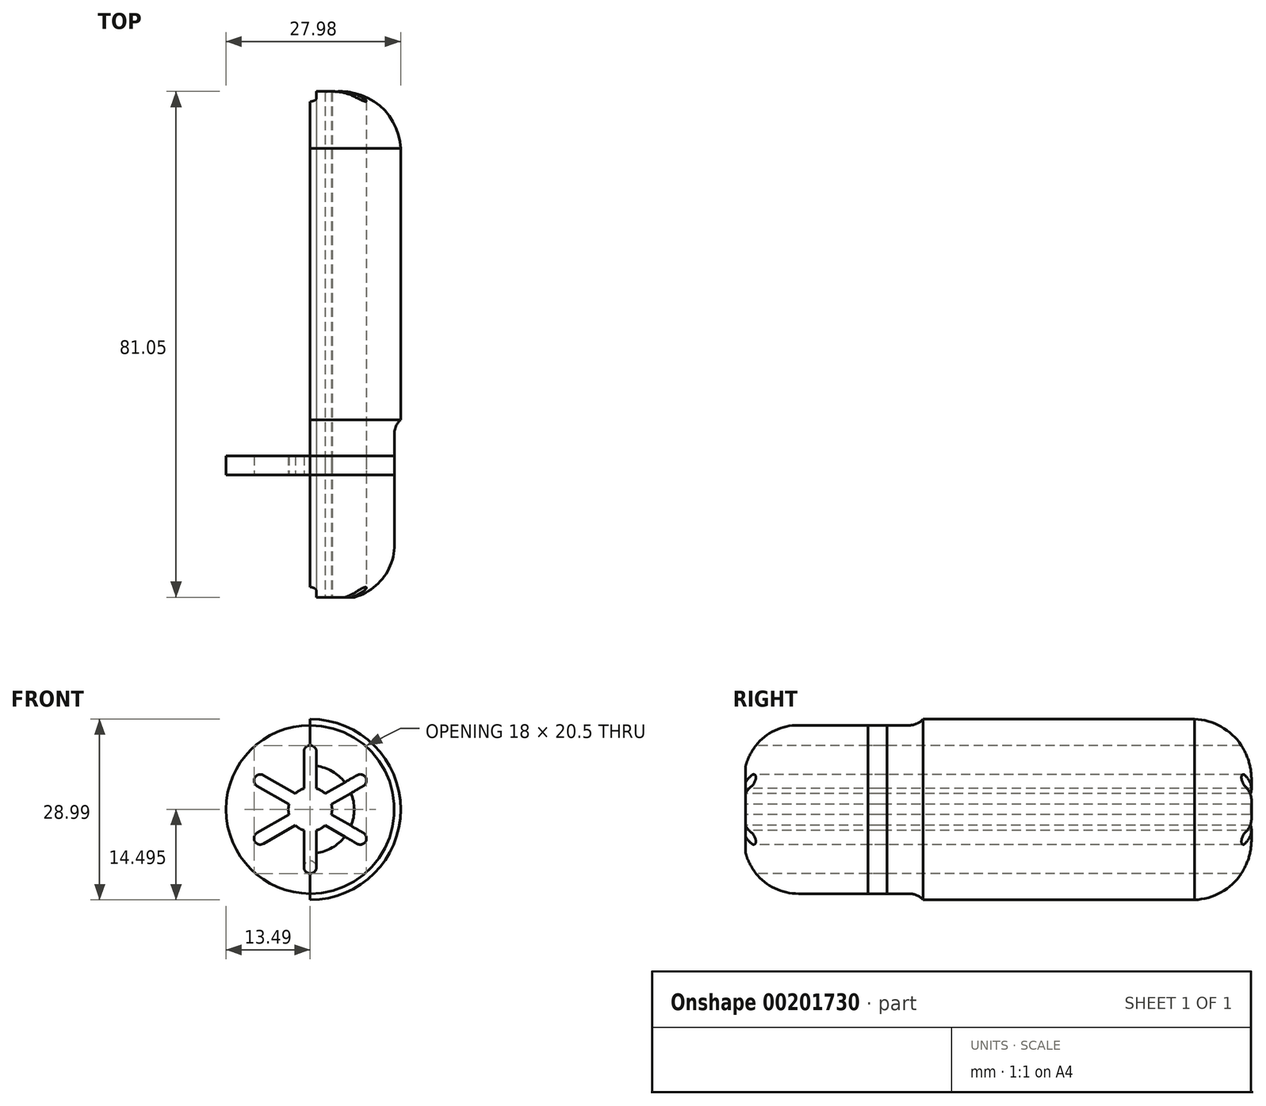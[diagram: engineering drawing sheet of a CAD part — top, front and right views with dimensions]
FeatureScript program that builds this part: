
annotation { "Feature Type Name" : "Feature", "Feature Type Description" : "" }
export const myFeature = defineFeature(function(context is Context, id is Id, definition is map)
    precondition{}
    {
        {
            var Q0;
            Q0=qCreatedBy(makeId("Right.planeOp"),FACE);
            var sketch = newSketch(context, id + "F0", { "sketchPlane" : qUnion([Q0])});
            skLineSegment(sketch, "E0.bottom", {"start": v(-3.13, 33.38) * mm, "end": v(86.87, 33.38) * mm});
            skLineSegment(sketch, "E0.top", {"start": v(-3.13, 32.38) * mm, "end": v(4.08, 32.38) * mm});
            skLineSegment(sketch, "E0.left", {"start": v(-3.13, 33.38) * mm, "end": v(-3.13, 32.38) * mm});
            skLineSegment(sketch, "E0.right", {"start": v(86.87, 33.38) * mm, "end": v(86.87, 32.38) * mm});
            skPoint(sketch, "E0.middle", {"position": v(41.87, 32.88) * mm});
            skLineSegment(sketch, "E1.bottom", {"start": v(86.87, 32.38) * mm, "end": v(81.87, 32.38) * mm, "construction": true});
            skLineSegment(sketch, "E1.top", {"start": v(86.87, 21.38) * mm, "end": v(85.87, 21.38) * mm});
            skLineSegment(sketch, "E1.left", {"start": v(86.87, 32.38) * mm, "end": v(86.87, 21.38) * mm, "construction": true});
            skLineSegment(sketch, "E1.right", {"start": v(81.87, 32.38) * mm, "end": v(81.87, 21.38) * mm, "construction": true});
            skLineSegment(sketch, "E2.bottom", {"start": v(81.87, 32.38) * mm, "end": v(71.87, 32.38) * mm, "construction": true});
            skLineSegment(sketch, "E2.top", {"start": v(81.87, 21.38) * mm, "end": v(71.87, 21.38) * mm, "construction": true});
            skLineSegment(sketch, "E2.right", {"start": v(71.87, 33.38) * mm, "end": v(71.87, 21.38) * mm, "construction": true});
            skLineSegment(sketch, "E3.0", {"start": v(85.87, 22.38) * mm, "end": v(85.37, 22.38) * mm, "construction": true});
            skLineSegment(sketch, "E4.0", {"start": v(85.87, 32.38) * mm, "end": v(85.87, 21.38) * mm, "construction": true});
            skArc(sketch, "E5", {"start": v(82.3, 22.38) * mm, "mid": v(80.84, 28.3) * mm, "end": v(76.33, 32.38) * mm});
            skArc(sketch, "E6", {"start": v(81.87, 21.38) * mm, "mid": v(79.3, 29.1) * mm, "end": v(71.87, 32.38) * mm});
            skLineSegment(sketch, "E7.trimOffspring", {"start": v(76.33, 32.38) * mm, "end": v(86.87, 32.38) * mm});
            skLineSegment(sketch, "E8.top", {"start": v(86.87, 25.38) * mm, "end": v(85.87, 25.38) * mm});
            skLineSegment(sketch, "E8.left", {"start": v(86.87, 23.38) * mm, "end": v(86.87, 25.38) * mm});
            skLineSegment(sketch, "E8.right", {"start": v(85.87, 22.38) * mm, "end": v(85.87, 22.72) * mm, "construction": true});
            skLineSegment(sketch, "E9.bottom", {"start": v(-3.13, 32.38) * mm, "end": v(-2.13, 32.38) * mm, "construction": true});
            skLineSegment(sketch, "E9.top", {"start": v(-3.13, 21.38) * mm, "end": v(-2.13, 21.38) * mm});
            skLineSegment(sketch, "E9.left", {"start": v(-3.13, 32.38) * mm, "end": v(-3.13, 21.38) * mm, "construction": true});
            skLineSegment(sketch, "E9.right", {"start": v(-2.13, 32.38) * mm, "end": v(-2.13, 21.38) * mm, "construction": true});
            skLineSegment(sketch, "E10.bottom", {"start": v(-2.13, 32.38) * mm, "end": v(4.08, 32.38) * mm, "construction": true});
            skLineSegment(sketch, "E10.top", {"start": v(-2.13, 33.38) * mm, "end": v(8.87, 33.38) * mm, "construction": true});
            skLineSegment(sketch, "E10.left", {"start": v(-2.13, 32.38) * mm, "end": v(-2.13, 33.38) * mm, "construction": true});
            skLineSegment(sketch, "E10.right", {"start": v(8.87, 32.38) * mm, "end": v(8.87, 33.38) * mm, "construction": true});
            skArc(sketch, "E11", {"start": v(4.08, 32.38) * mm, "mid": v(-1.17, 27.96) * mm, "end": v(-3.13, 21.38) * mm});
            skArc(sketch, "E12", {"start": v(8.87, 32.38) * mm, "mid": v(1.1, 29.16) * mm, "end": v(-2.13, 21.38) * mm});
            skLineSegment(sketch, "E13.trimOffspring", {"start": v(8.87, 32.38) * mm, "end": v(71.87, 32.38) * mm});
            skLineSegment(sketch, "E14", {"start": v(8.87, 21.38) * mm, "end": v(71.87, 21.38) * mm, "construction": true});
            skLineSegment(sketch, "E15.0", {"start": v(8.87, 17.38) * mm, "end": v(71.87, 17.38) * mm, "construction": true});
            skLineSegment(sketch, "E16.0", {"start": v(86.87, 23.38) * mm, "end": v(85.87, 23.38) * mm, "construction": true});
            skLineSegment(sketch, "E17.0", {"start": v(83.87, 21.38) * mm, "end": v(83.87, 25.38) * mm, "construction": true});
            skLineSegment(sketch, "E18", {"start": v(86.87, 23.38) * mm, "end": v(83.87, 21.38) * mm});
            skLineSegment(sketch, "E19.0", {"start": v(85.87, 23.92) * mm, "end": v(83.57, 22.38) * mm});
            skLineSegment(sketch, "E20.trimOffspring", {"start": v(83.87, 21.38) * mm, "end": v(81.87, 21.38) * mm});
            skLineSegment(sketch, "E21.trimOffspring", {"start": v(83.57, 22.38) * mm, "end": v(82.3, 22.38) * mm});
            skLineSegment(sketch, "E22.trimOffspring", {"start": v(85.87, 23.92) * mm, "end": v(85.87, 25.38) * mm});
            skLineSegment(sketch, "E23.bottom", {"start": v(8.87, 17.38) * mm, "end": v(-3.13, 17.38) * mm, "construction": true});
            skLineSegment(sketch, "E23.top", {"start": v(8.87, 21.38) * mm, "end": v(-3.13, 21.38) * mm, "construction": true});
            skLineSegment(sketch, "E23.left", {"start": v(8.87, 17.38) * mm, "end": v(8.87, 21.38) * mm, "construction": true});
            skLineSegment(sketch, "E23.right", {"start": v(-3.13, 17.38) * mm, "end": v(-3.13, 21.38) * mm, "construction": true});
            skSolve(sketch);
        }
        {
            var Q0;
            Q0=qCreatedBy(makeId("Right.planeOp"),FACE);
            var sketch = newSketch(context, id + "F1", { "sketchPlane" : qUnion([Q0])});
            skLineSegment(sketch, "E24.bottom", {"start": v(-3.13, 33.38) * mm, "end": v(28.58, 33.38) * mm, "construction": true});
            skLineSegment(sketch, "E24.left", {"start": v(-3.13, 33.38) * mm, "end": v(-3.13, 23.38) * mm, "construction": true});
            skLineSegment(sketch, "E24.right", {"start": v(28.58, 33.38) * mm, "end": v(28.58, 33.38) * mm});
            skLineSegment(sketch, "E25", {"start": v(28.58, 32.38) * mm, "end": v(8.84, 32.38) * mm, "construction": true});
            skArc(sketch, "E26", {"start": v(8.84, 32.38) * mm, "mid": v(1.84, 29.83) * mm, "end": v(-1.88, 23.38) * mm, "construction": true});
            skLineSegment(sketch, "E27.0", {"start": v(27.9, 31.88) * mm, "end": v(8.84, 31.88) * mm});
            skArc(sketch, "E28.0", {"start": v(8.84, 31.88) * mm, "mid": v(2.16, 29.45) * mm, "end": v(-1.38, 23.3) * mm});
            skLineSegment(sketch, "E29.0", {"start": v(26.58, 31.38) * mm, "end": v(8.84, 31.38) * mm});
            skArc(sketch, "E30.0", {"start": v(8.84, 30.88) * mm, "mid": v(2.9, 28.77) * mm, "end": v(-0.35, 23.38) * mm, "construction": true});
            skPoint(sketch, "E31.newPointB", {"position": v(28.58, 23.38) * mm});
            skArc(sketch, "E31.filletArc", {"start": v(26.58, 31.38) * mm, "mid": v(27.3, 31.5) * mm, "end": v(27.9, 31.88) * mm});
            skArc(sketch, "E32", {"start": v(8.84, 31.38) * mm, "mid": v(2.64, 29.01) * mm, "end": v(-0.4, 23.12) * mm});
            skLineSegment(sketch, "E33.trimOffspring", {"start": v(-1.37, 23.38) * mm, "end": v(-0.35, 23.38) * mm});
            skSolve(sketch);
        }
        {
            var Q0;
            Q0=qCreatedBy(makeId("Right.planeOp"),FACE);
            var sketch = newSketch(context, id + "F2", { "sketchPlane" : qUnion([Q0])});
            skLineSegment(sketch, "E34", {"start": v(86.87, 23.38) * mm, "end": v(83.87, 21.38) * mm, "construction": true});
            skLineSegment(sketch, "E35", {"start": v(83.87, 21.38) * mm, "end": v(81.87, 21.38) * mm, "construction": true});
            skLineSegment(sketch, "E36.0", {"start": v(86.87, 22.78) * mm, "end": v(84.02, 20.88) * mm});
            skLineSegment(sketch, "E37.0", {"start": v(84.02, 20.88) * mm, "end": v(81.87, 20.88) * mm});
            skLineSegment(sketch, "E38", {"start": v(86.87, 22.78) * mm, "end": v(86.87, 17.38) * mm});
            skLineSegment(sketch, "E39.0", {"start": v(66.87, 20.38) * mm, "end": v(66.87, 17.38) * mm});
            skLineSegment(sketch, "E40.0", {"start": v(81.87, 20.38) * mm, "end": v(66.87, 20.38) * mm});
            skLineSegment(sketch, "E41", {"start": v(71.87, 17.38) * mm, "end": v(66.87, 17.38) * mm});
            skLineSegment(sketch, "E42", {"start": v(71.87, 17.38) * mm, "end": v(86.87, 17.38) * mm});
            skLineSegment(sketch, "E43.0", {"start": v(81.87, 20.88) * mm, "end": v(81.87, 20.38) * mm});
            skSolve(sketch);
        }
        {
            var Q0;
            Q0=qCreatedBy(makeId("Right.planeOp"),FACE);
            var sketch = newSketch(context, id + "F3", { "sketchPlane" : qUnion([Q0])});
            skArc(sketch, "E44", {"start": v(81.87, 21.38) * mm, "mid": v(79.3, 29.1) * mm, "end": v(71.87, 32.38) * mm, "construction": true});
            skArc(sketch, "E45.0", {"start": v(81.3, 20.88) * mm, "mid": v(79.25, 28.4) * mm, "end": v(72.28, 31.88) * mm});
            skLineSegment(sketch, "E46", {"start": v(81.87, 20.38) * mm, "end": v(69.18, 20.38) * mm, "construction": true});
            skLineSegment(sketch, "E47", {"start": v(28.58, 32.38) * mm, "end": v(37.05, 32.38) * mm});
            skLineSegment(sketch, "E48", {"start": v(26.58, 31.38) * mm, "end": v(22.5, 31.38) * mm});
            skArc(sketch, "E49", {"start": v(26.58, 31.38) * mm, "mid": v(27.7, 31.64) * mm, "end": v(28.58, 32.38) * mm});
            skLineSegment(sketch, "E50.0", {"start": v(28.58, 31.88) * mm, "end": v(72.28, 31.88) * mm});
            skArc(sketch, "E51.0", {"start": v(26.58, 30.88) * mm, "mid": v(27.93, 31.2) * mm, "end": v(28.98, 32.08) * mm});
            skLineSegment(sketch, "E52.0", {"start": v(26.58, 30.88) * mm, "end": v(8.74, 30.88) * mm});
            skLineSegment(sketch, "E53.0", {"start": v(81.3, 20.88) * mm, "end": v(0.37, 20.88) * mm});
            skArc(sketch, "E54", {"start": v(8.84, 31.38) * mm, "mid": v(2.74, 29.11) * mm, "end": v(-0.35, 23.38) * mm, "construction": true});
            skArc(sketch, "E55.0", {"start": v(8.83, 30.88) * mm, "mid": v(3.5, 29.1) * mm, "end": v(0.37, 24.44) * mm});
            skLineSegment(sketch, "E56", {"start": v(-2.13, 27.58) * mm, "end": v(-2.13, 15.19) * mm, "construction": true});
            skLineSegment(sketch, "E57.trimOffspring", {"start": v(0.37, 24.44) * mm, "end": v(0.37, 20.88) * mm});
            skSolve(sketch);
        }
        {
            var Q0;
            Q0=qSketchRegion(id+"F3",true);
            var Q1;
            Q1=sQuery(id+"F0.wireOp",EDGE,"E15.0");
            revolve(context, id + "F4", {"entities" : qUnion([Q0]), "axis" : qUnion([Q1]), "revolveType" : RevolveType.ONE_DIRECTION, "angle" : 180 * degree});
        }
        {
            var Q0;
            Q0=qCreatedBy(makeId("Front.planeOp"),FACE);
            var sketch = newSketch(context, id + "F5", { "sketchPlane" : qUnion([Q0])});
            skCircle(sketch, "E58", {"center": v(0, 17.38) * mm, "radius": 14.5 * mm, "construction": true});
            skCircle(sketch, "E59", {"center": v(0, 17.38) * mm, "radius": 3.5 * mm});
            skLineSegment(sketch, "E60", {"start": v(0, 17.38) * mm, "end": v(0, 4.9) * mm, "construction": true});
            skPoint(sketch, "E61", {"position": v(0, 4.9) * mm});
            skPoint(sketch, "E62", {"position": v(-16.26, 26.77) * mm});
            skLineSegment(sketch, "E63.0", {"start": v(-1, 14.03) * mm, "end": v(-1, 8.13) * mm});
            skLineSegment(sketch, "E64.0", {"start": v(1, 14.03) * mm, "end": v(1, 8.13) * mm});
            skLineSegment(sketch, "E65", {"start": v(0, 7.13) * mm, "end": v(0, 7.13) * mm});
            skPoint(sketch, "E66.visualSharp", {"position": v(-1, 7.13) * mm});
            skArc(sketch, "E66.filletArc", {"start": v(-1, 8.13) * mm, "mid": v(-0.7, 7.43) * mm, "end": v(0, 7.13) * mm});
            skPoint(sketch, "E67.visualSharp", {"position": v(1, 7.13) * mm});
            skArc(sketch, "E67.filletArc", {"start": v(0, 7.13) * mm, "mid": v(0.7, 7.43) * mm, "end": v(1, 8.13) * mm});
            skSolve(sketch);
        }
        {
            var Q0;
            {var subQ0=sQuery(id+"F5.wireOp",EDGE,"E63.0");Q0=makeQuery(id+"F5.imprint","IMPRINT",FACE,{"disambiguationData":[TD([[makeQuery(id+"F5.imprint","IMPRINT",EDGE,{"derivedFrom":subQ0}),1.0]])]});}
            extrude(context, id + "F6", {"entities" : qUnion([Q0]), "oppositeDirection" : true, "depth" : 90 * mm});
        }
        {
            var Q0;
            Q0=qCreatedBy(makeId("Right.planeOp"),FACE);
            var sketch = newSketch(context, id + "F7", { "sketchPlane" : qUnion([Q0])});
            skLineSegment(sketch, "E68", {"start": v(0, 17.38) * mm, "end": v(41.07, 17.38) * mm});
            skSolve(sketch);
        }
        {
            var Q0;
            Q0=makeQuery(id+"F6.opExtrude","SWEPT_BODY",BODY,{"disambiguationData":[OSD([sQuery(id+"F5.wireOp",EDGE,"E59"),sQuery(id+"F5.wireOp",EDGE,"E63.0"),sQuery(id+"F5.wireOp",EDGE,"E64.0"),sQuery(id+"F5.wireOp",EDGE,"c18d3147-b101-4655-83fc-4fb6f8fd4f04")])]});
            var Q1;
            Q1=sQuery(id+"F7.wireOp",EDGE,"E68");
            circularPattern(context, id + "F8", {"entities" : qUnion([Q0]), "axis" : qUnion([Q1]), "angle" : 360 * degree, "instanceCount" : 6, "equalSpace" : true});
        }
        {
            var Q0;
            Q0=makeQuery(id+"F6.opExtrude","SWEPT_BODY",BODY,{"disambiguationData":[OSD([sQuery(id+"F5.wireOp",EDGE,"E59"),sQuery(id+"F5.wireOp",EDGE,"E63.0"),sQuery(id+"F5.wireOp",EDGE,"E64.0"),sQuery(id+"F5.wireOp",EDGE,"E66.filletArc"),sQuery(id+"F5.wireOp",EDGE,"E67.filletArc")])]});
            var Q1;
            Q1=makeQuery(id+"F8.opPattern","COPY",BODY,{"derivedFrom":makeQuery(id+"F6.opExtrude","SWEPT_BODY",BODY,{"disambiguationData":[OSD([sQuery(id+"F5.wireOp",EDGE,"E59"),sQuery(id+"F5.wireOp",EDGE,"E63.0"),sQuery(id+"F5.wireOp",EDGE,"E64.0"),sQuery(id+"F5.wireOp",EDGE,"E66.filletArc"),sQuery(id+"F5.wireOp",EDGE,"E67.filletArc")])]}),"instanceName":"5"});
            var Q2;
            Q2=makeQuery(id+"F8.opPattern","COPY",BODY,{"derivedFrom":makeQuery(id+"F6.opExtrude","SWEPT_BODY",BODY,{"disambiguationData":[OSD([sQuery(id+"F5.wireOp",EDGE,"E59"),sQuery(id+"F5.wireOp",EDGE,"E63.0"),sQuery(id+"F5.wireOp",EDGE,"E64.0"),sQuery(id+"F5.wireOp",EDGE,"E66.filletArc"),sQuery(id+"F5.wireOp",EDGE,"E67.filletArc")])]}),"instanceName":"4"});
            var Q3;
            Q3=makeQuery(id+"F8.opPattern","COPY",BODY,{"derivedFrom":makeQuery(id+"F6.opExtrude","SWEPT_BODY",BODY,{"disambiguationData":[OSD([sQuery(id+"F5.wireOp",EDGE,"E59"),sQuery(id+"F5.wireOp",EDGE,"E63.0"),sQuery(id+"F5.wireOp",EDGE,"E64.0"),sQuery(id+"F5.wireOp",EDGE,"E66.filletArc"),sQuery(id+"F5.wireOp",EDGE,"E67.filletArc")])]}),"instanceName":"3"});
            var Q4;
            Q4=makeQuery(id+"F4.opRevolve","SWEPT_BODY",BODY,{"disambiguationData":[OSD([sQuery(id+"F3.wireOp",EDGE,"E45.0"),sQuery(id+"F3.wireOp",EDGE,"E50.0"),sQuery(id+"F3.wireOp",EDGE,"E51.0"),sQuery(id+"F3.wireOp",EDGE,"E52.0"),sQuery(id+"F3.wireOp",EDGE,"E53.0"),sQuery(id+"F3.wireOp",EDGE,"E55.0"),sQuery(id+"F3.wireOp",EDGE,"E57.trimOffspring")])]});
            booleanBodies(context, id + "F9", {"operationType" : BooleanOperationType.SUBTRACTION, "tools" : qUnion([Q0, Q1, Q2, Q3]), "targets" : qUnion([Q4]), "keepTools" : true});
        }
        {
            var Q0;
            Q0 = qSketchRegion(id + "F3", true);
            var Q1;
            Q1=sQuery(id+"F0.wireOp",EDGE,"E15.0");
            revolve(context, id + "F10", {"entities" : qUnion([Q0]), "axis" : qUnion([Q1]), "revolveType" : RevolveType.FULL});
        }
        {
            var Q0;
            Q0=qCreatedBy(makeId("Front.planeOp"),FACE);
            var sketch = newSketch(context, id + "F11", { "sketchPlane" : qUnion([Q0])});
            skCircle(sketch, "E69.0", {"center": v(0, 17.38) * mm, "radius": 13.5 * mm});
            skSolve(sketch);
        }
        {
            var Q0;
            Q0=makeQuery(id+"F11.imprint","IMPRINT",FACE,{"disambiguationData":[TD([[makeQuery(id+"F11.imprint","IMPRINT",EDGE,{"derivedFrom":sQuery(id+"F11.wireOp",EDGE,"E69.0")}),1.0]])]});
            extrude(context, id + "F12", {"entities" : qUnion([Q0]), "oppositeDirection" : true, "depth" : 23 * mm, "hasSecondDirection" : true, "secondDirectionOppositeDirection" : true, "secondDirectionDepth" : 20 * mm});
        }
        {
            var Q0;
            Q0=makeQuery(id+"F6.opExtrude","SWEPT_BODY",BODY,{"disambiguationData":[OSD([sQuery(id+"F5.wireOp",EDGE,"E59"),sQuery(id+"F5.wireOp",EDGE,"E63.0"),sQuery(id+"F5.wireOp",EDGE,"E64.0"),sQuery(id+"F5.wireOp",EDGE,"E66.filletArc"),sQuery(id+"F5.wireOp",EDGE,"E67.filletArc")])]});
            var Q1;
            Q1=makeQuery(id+"F8.opPattern","COPY",BODY,{"derivedFrom":makeQuery(id+"F6.opExtrude","SWEPT_BODY",BODY,{"disambiguationData":[OSD([sQuery(id+"F5.wireOp",EDGE,"E59"),sQuery(id+"F5.wireOp",EDGE,"E63.0"),sQuery(id+"F5.wireOp",EDGE,"E64.0"),sQuery(id+"F5.wireOp",EDGE,"E66.filletArc"),sQuery(id+"F5.wireOp",EDGE,"E67.filletArc")])]}),"instanceName":"5"});
            var Q2;
            Q2=makeQuery(id+"F8.opPattern","COPY",BODY,{"derivedFrom":makeQuery(id+"F6.opExtrude","SWEPT_BODY",BODY,{"disambiguationData":[OSD([sQuery(id+"F5.wireOp",EDGE,"E59"),sQuery(id+"F5.wireOp",EDGE,"E63.0"),sQuery(id+"F5.wireOp",EDGE,"E64.0"),sQuery(id+"F5.wireOp",EDGE,"E66.filletArc"),sQuery(id+"F5.wireOp",EDGE,"E67.filletArc")])]}),"instanceName":"4"});
            var Q3;
            Q3=makeQuery(id+"F8.opPattern","COPY",BODY,{"derivedFrom":makeQuery(id+"F6.opExtrude","SWEPT_BODY",BODY,{"disambiguationData":[OSD([sQuery(id+"F5.wireOp",EDGE,"E59"),sQuery(id+"F5.wireOp",EDGE,"E63.0"),sQuery(id+"F5.wireOp",EDGE,"E64.0"),sQuery(id+"F5.wireOp",EDGE,"E66.filletArc"),sQuery(id+"F5.wireOp",EDGE,"E67.filletArc")])]}),"instanceName":"3"});
            var Q4;
            Q4=makeQuery(id+"F8.opPattern","COPY",BODY,{"derivedFrom":makeQuery(id+"F6.opExtrude","SWEPT_BODY",BODY,{"disambiguationData":[OSD([sQuery(id+"F5.wireOp",EDGE,"E59"),sQuery(id+"F5.wireOp",EDGE,"E63.0"),sQuery(id+"F5.wireOp",EDGE,"E64.0"),sQuery(id+"F5.wireOp",EDGE,"E66.filletArc"),sQuery(id+"F5.wireOp",EDGE,"E67.filletArc")])]}),"instanceName":"2"});
            var Q5;
            Q5=makeQuery(id+"F8.opPattern","COPY",BODY,{"derivedFrom":makeQuery(id+"F6.opExtrude","SWEPT_BODY",BODY,{"disambiguationData":[OSD([sQuery(id+"F5.wireOp",EDGE,"E59"),sQuery(id+"F5.wireOp",EDGE,"E63.0"),sQuery(id+"F5.wireOp",EDGE,"E64.0"),sQuery(id+"F5.wireOp",EDGE,"E66.filletArc"),sQuery(id+"F5.wireOp",EDGE,"E67.filletArc")])]}),"instanceName":"1"});
            var Q6;
            Q6=makeQuery(id+"F10.opRevolve","SWEPT_BODY",BODY,{"disambiguationData":[OSD([sQuery(id+"F3.wireOp",EDGE,"E45.0"),sQuery(id+"F3.wireOp",EDGE,"E50.0"),sQuery(id+"F3.wireOp",EDGE,"E51.0"),sQuery(id+"F3.wireOp",EDGE,"E52.0"),sQuery(id+"F3.wireOp",EDGE,"E53.0"),sQuery(id+"F3.wireOp",EDGE,"E55.0"),sQuery(id+"F3.wireOp",EDGE,"E57.trimOffspring")])]});
            booleanBodies(context, id + "F13", {"operationType" : BooleanOperationType.SUBTRACTION, "tools" : qUnion([Q0, Q1, Q2, Q3, Q4, Q5]), "targets" : qUnion([Q6])});
        }
        {
            var Q0;
            Q0=makeQuery(id+"F10.opRevolve","SWEPT_BODY",BODY,{"disambiguationData":[OSD([sQuery(id+"F3.wireOp",EDGE,"E45.0"),sQuery(id+"F3.wireOp",EDGE,"E50.0"),sQuery(id+"F3.wireOp",EDGE,"E51.0"),sQuery(id+"F3.wireOp",EDGE,"E52.0"),sQuery(id+"F3.wireOp",EDGE,"E53.0"),sQuery(id+"F3.wireOp",EDGE,"E55.0"),sQuery(id+"F3.wireOp",EDGE,"E57.trimOffspring")])]});
            var Q1;
            Q1=makeQuery(id+"F12.opExtrude","SWEPT_BODY",BODY,{"disambiguationData":[OSD([sQuery(id+"F11.wireOp",EDGE,"E69.0")])]});
            booleanBodies(context, id + "F14", {"operationType" : BooleanOperationType.INTERSECTION, "tools" : qUnion([Q0, Q1])});
        }
    });
